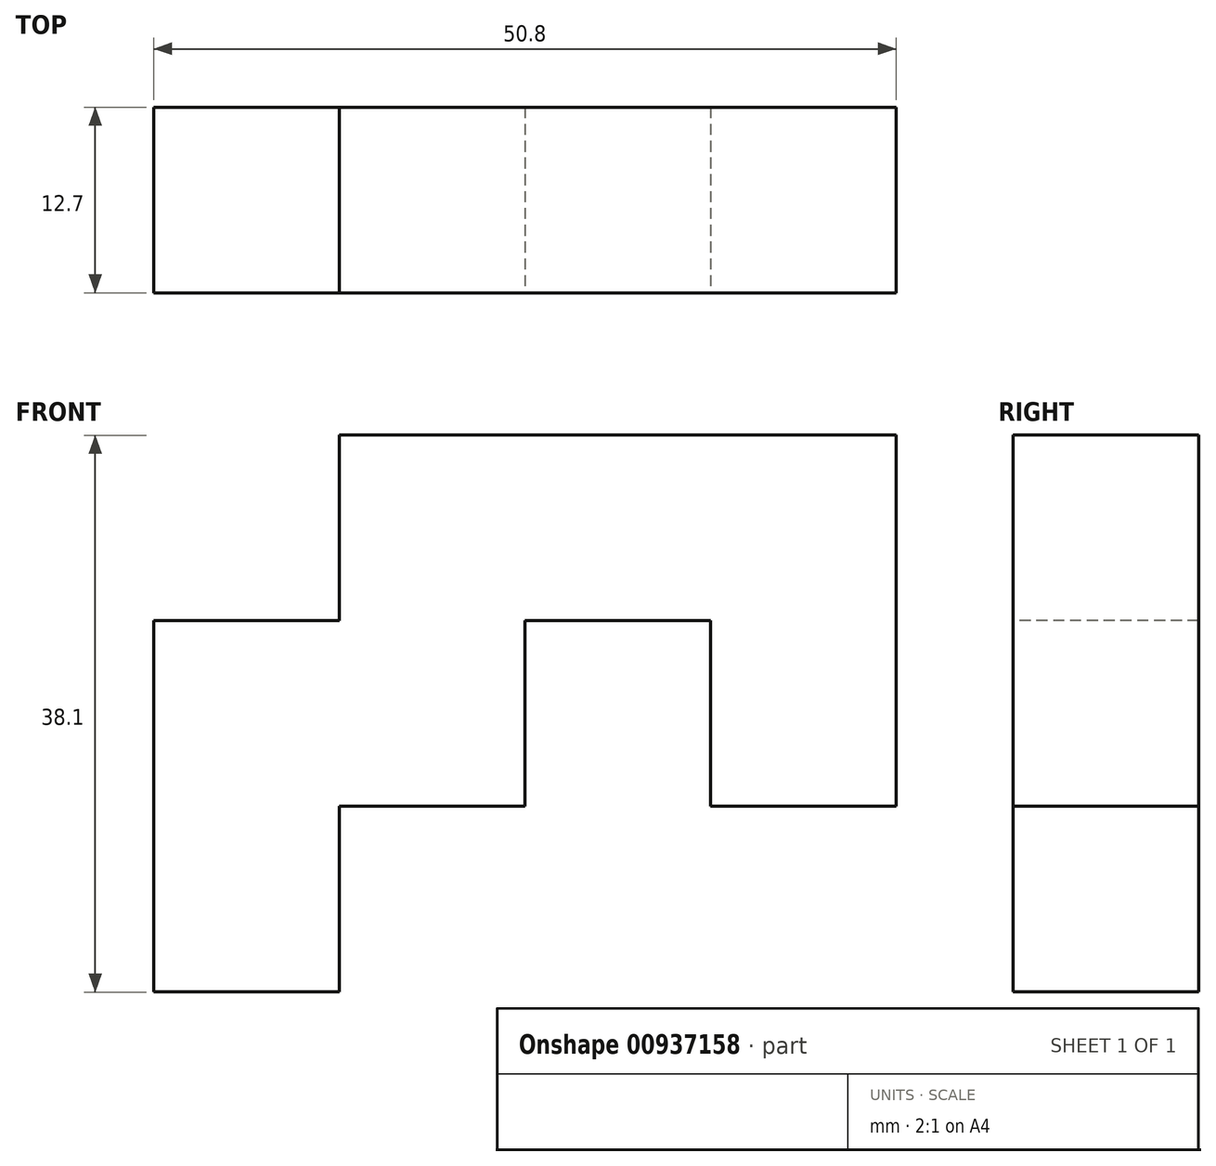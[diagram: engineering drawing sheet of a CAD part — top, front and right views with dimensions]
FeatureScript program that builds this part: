
annotation { "Feature Type Name" : "Feature", "Feature Type Description" : "" }
export const myFeature = defineFeature(function(context is Context, id is Id, definition is map)
    precondition{}
    {
        {
            var Q0;
            Q0=qCreatedBy(makeId("Front.planeOp"),FACE);
            var sketch = newSketch(context, id + "F0", { "sketchPlane" : qUnion([Q0])});
            skLineSegment(sketch, "E0.bottom", {"start": v(-62.43, 23.8) * mm, "end": v(-49.73, 23.8) * mm});
            skLineSegment(sketch, "E0.top", {"start": v(-62.43, 36.5) * mm, "end": v(-49.73, 36.5) * mm});
            skLineSegment(sketch, "E0.left", {"start": v(-62.43, 23.8) * mm, "end": v(-62.43, 36.5) * mm});
            skLineSegment(sketch, "E0.right", {"start": v(-49.73, 23.8) * mm, "end": v(-49.73, 36.5) * mm});
            skLineSegment(sketch, "E1.top", {"start": v(-62.43, 49.2) * mm, "end": v(-49.73, 49.2) * mm});
            skLineSegment(sketch, "E1.left", {"start": v(-62.43, 36.5) * mm, "end": v(-62.43, 49.2) * mm});
            skLineSegment(sketch, "E1.right", {"start": v(-49.73, 36.5) * mm, "end": v(-49.73, 49.2) * mm});
            skLineSegment(sketch, "E2.bottom", {"start": v(-49.73, 49.2) * mm, "end": v(-37.03, 49.2) * mm});
            skLineSegment(sketch, "E2.top", {"start": v(-49.73, 36.5) * mm, "end": v(-37.03, 36.5) * mm});
            skLineSegment(sketch, "E2.left", {"start": v(-49.73, 49.2) * mm, "end": v(-49.73, 36.5) * mm});
            skLineSegment(sketch, "E2.right", {"start": v(-37.03, 49.2) * mm, "end": v(-37.03, 36.5) * mm});
            skLineSegment(sketch, "E3.top", {"start": v(-49.73, 61.9) * mm, "end": v(-37.03, 61.9) * mm});
            skLineSegment(sketch, "E3.left", {"start": v(-49.73, 49.2) * mm, "end": v(-49.73, 61.9) * mm});
            skLineSegment(sketch, "E3.right", {"start": v(-37.03, 49.2) * mm, "end": v(-37.03, 61.9) * mm});
            skLineSegment(sketch, "E4.bottom", {"start": v(-37.03, 61.9) * mm, "end": v(-24.33, 61.9) * mm});
            skLineSegment(sketch, "E4.top", {"start": v(-37.03, 49.2) * mm, "end": v(-24.33, 49.2) * mm});
            skLineSegment(sketch, "E4.left", {"start": v(-37.03, 61.9) * mm, "end": v(-37.03, 49.2) * mm});
            skLineSegment(sketch, "E4.right", {"start": v(-24.33, 61.9) * mm, "end": v(-24.33, 49.2) * mm});
            skLineSegment(sketch, "E5.bottom", {"start": v(-24.33, 61.9) * mm, "end": v(-11.63, 61.9) * mm});
            skLineSegment(sketch, "E5.top", {"start": v(-24.33, 49.2) * mm, "end": v(-11.63, 49.2) * mm});
            skLineSegment(sketch, "E5.right", {"start": v(-11.63, 61.9) * mm, "end": v(-11.63, 49.2) * mm});
            skLineSegment(sketch, "E6.top", {"start": v(-24.33, 36.5) * mm, "end": v(-11.63, 36.5) * mm});
            skLineSegment(sketch, "E6.left", {"start": v(-24.33, 49.2) * mm, "end": v(-24.33, 36.5) * mm});
            skLineSegment(sketch, "E6.right", {"start": v(-11.63, 49.2) * mm, "end": v(-11.63, 36.5) * mm});
            skSolve(sketch);
        }
        {
            var Q0;
            Q0 = qSketchRegion(id + "F0", true);
            extrude(context, id + "F1", {"entities" : qUnion([Q0]), "oppositeDirection" : true, "depth" : 12.7 * mm, "offsetDistance" : 25.4 * mm});
        }
    });
